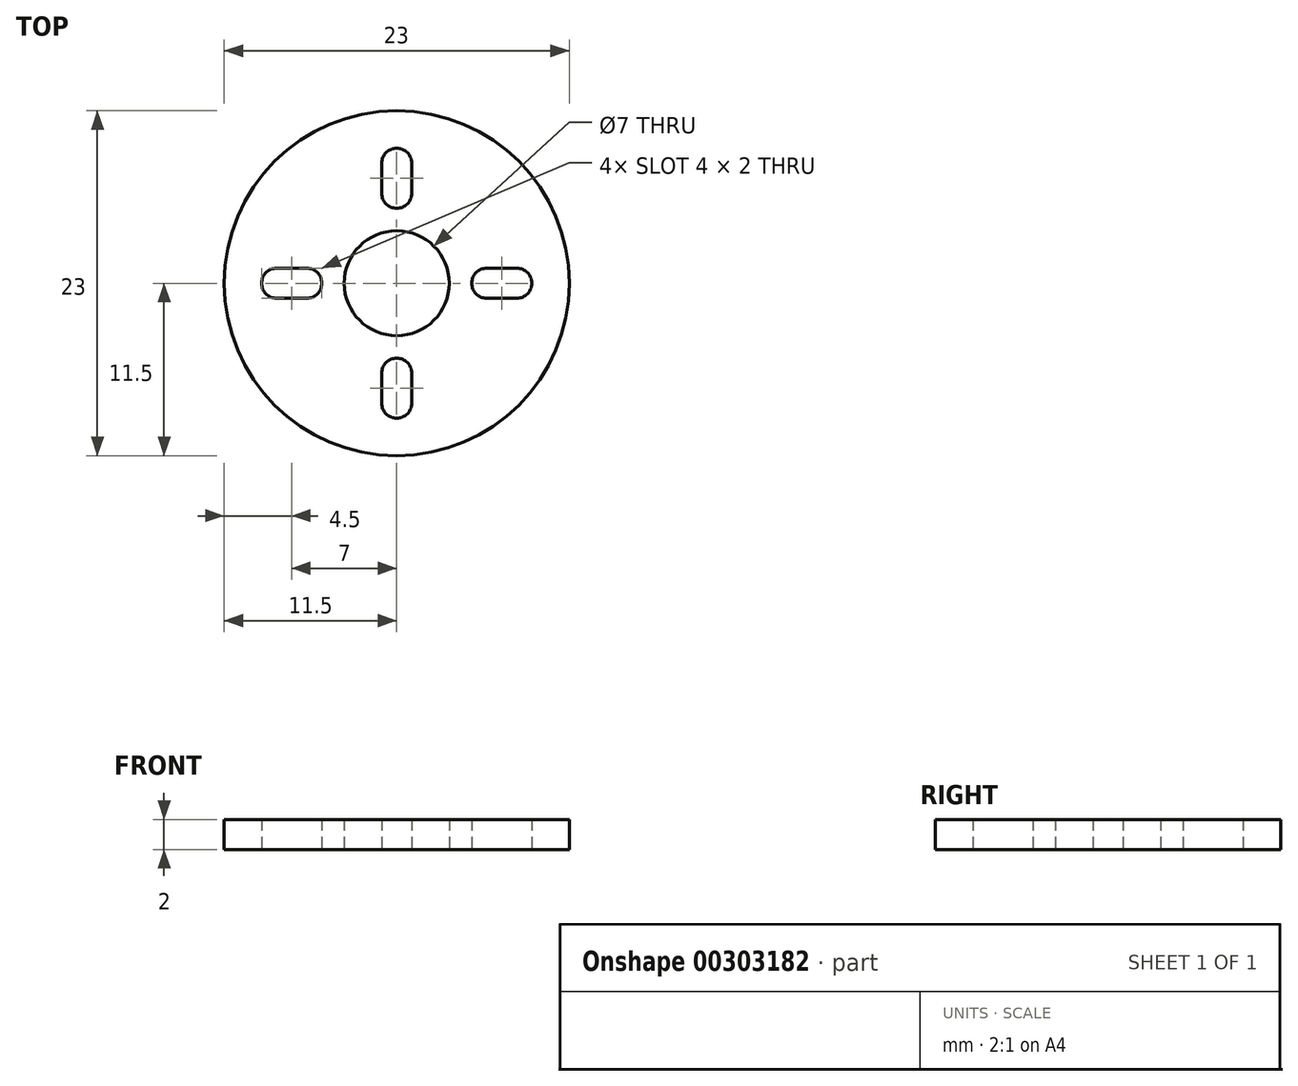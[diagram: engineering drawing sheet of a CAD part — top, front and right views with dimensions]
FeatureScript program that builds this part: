
annotation { "Feature Type Name" : "Feature", "Feature Type Description" : "" }
export const myFeature = defineFeature(function(context is Context, id is Id, definition is map)
    precondition{}
    {
        {
            var Q0;
            Q0=qCreatedBy(makeId("Top.planeOp"),FACE);
            var sketch = newSketch(context, id + "F0", { "sketchPlane" : qUnion([Q0])});
            skCircle(sketch, "E0", {"center": v(0, 0) * mm, "radius": 3.5 * mm});
            skCircle(sketch, "E1", {"center": v(0, 0) * mm, "radius": 6 * mm, "construction": true});
            skCircle(sketch, "E2", {"center": v(0, 0) * mm, "radius": 8 * mm, "construction": true});
            skLineSegment(sketch, "E3", {"start": v(0, 0) * mm, "end": v(-6, 0) * mm, "construction": true});
            skLineSegment(sketch, "E4", {"start": v(-8, 0) * mm, "end": v(-16.7, 0) * mm, "construction": true});
            skLineSegment(sketch, "E5", {"start": v(-6, 0) * mm, "end": v(-8, 0) * mm, "construction": true});
            skArc(sketch, "E6.0.startCap", {"start": v(-6, 1) * mm, "mid": v(-5, 0) * mm, "end": v(-6, -1) * mm});
            skArc(sketch, "E6.0.endCap", {"start": v(-8, -1) * mm, "mid": v(-9, 0) * mm, "end": v(-8, 1) * mm});
            skLineSegment(sketch, "E6.0.left", {"start": v(-6, -1) * mm, "end": v(-8, -1) * mm});
            skLineSegment(sketch, "E6.0.right", {"start": v(-6, 1) * mm, "end": v(-8, 1) * mm});
            skArc(sketch, "E7.1.0", {"start": v(1, -8) * mm, "mid": v(0, -9) * mm, "end": v(-1, -8) * mm});
            skLineSegment(sketch, "E7.1.1", {"start": v(-1, -6) * mm, "end": v(-1, -8) * mm});
            skArc(sketch, "E7.1.2", {"start": v(-1, -6) * mm, "mid": v(0, -5) * mm, "end": v(1, -6) * mm});
            skLineSegment(sketch, "E7.1.3", {"start": v(1, -6) * mm, "end": v(1, -8) * mm});
            skArc(sketch, "E7.2.0", {"start": v(8, 1) * mm, "mid": v(9, 0) * mm, "end": v(8, -1) * mm});
            skLineSegment(sketch, "E7.2.1", {"start": v(6, -1) * mm, "end": v(8, -1) * mm});
            skArc(sketch, "E7.2.2", {"start": v(6, -1) * mm, "mid": v(5, 0) * mm, "end": v(6, 1) * mm});
            skLineSegment(sketch, "E7.2.3", {"start": v(6, 1) * mm, "end": v(8, 1) * mm});
            skArc(sketch, "E7.3.0", {"start": v(-1, 8) * mm, "mid": v(0, 9) * mm, "end": v(1, 8) * mm});
            skLineSegment(sketch, "E7.3.1", {"start": v(1, 6) * mm, "end": v(1, 8) * mm});
            skArc(sketch, "E7.3.2", {"start": v(1, 6) * mm, "mid": v(0, 5) * mm, "end": v(-1, 6) * mm});
            skLineSegment(sketch, "E7.3.3", {"start": v(-1, 6) * mm, "end": v(-1, 8) * mm});
            skCircle(sketch, "E8", {"center": v(0, 0) * mm, "radius": 11.5 * mm});
            skSolve(sketch);
        }
        {
            var Q0;
            Q0=makeQuery(id+"F0.imprint","IMPRINT",FACE,{"disambiguationData":[TD([[makeQuery(id+"F0.imprint","IMPRINT",EDGE,{"derivedFrom":sQuery(id+"F0.wireOp",EDGE,"E0")}),-1.0]])]});
            extrude(context, id + "F1", {"entities" : qUnion([Q0]), "depth" : 2 * mm});
        }
    });
